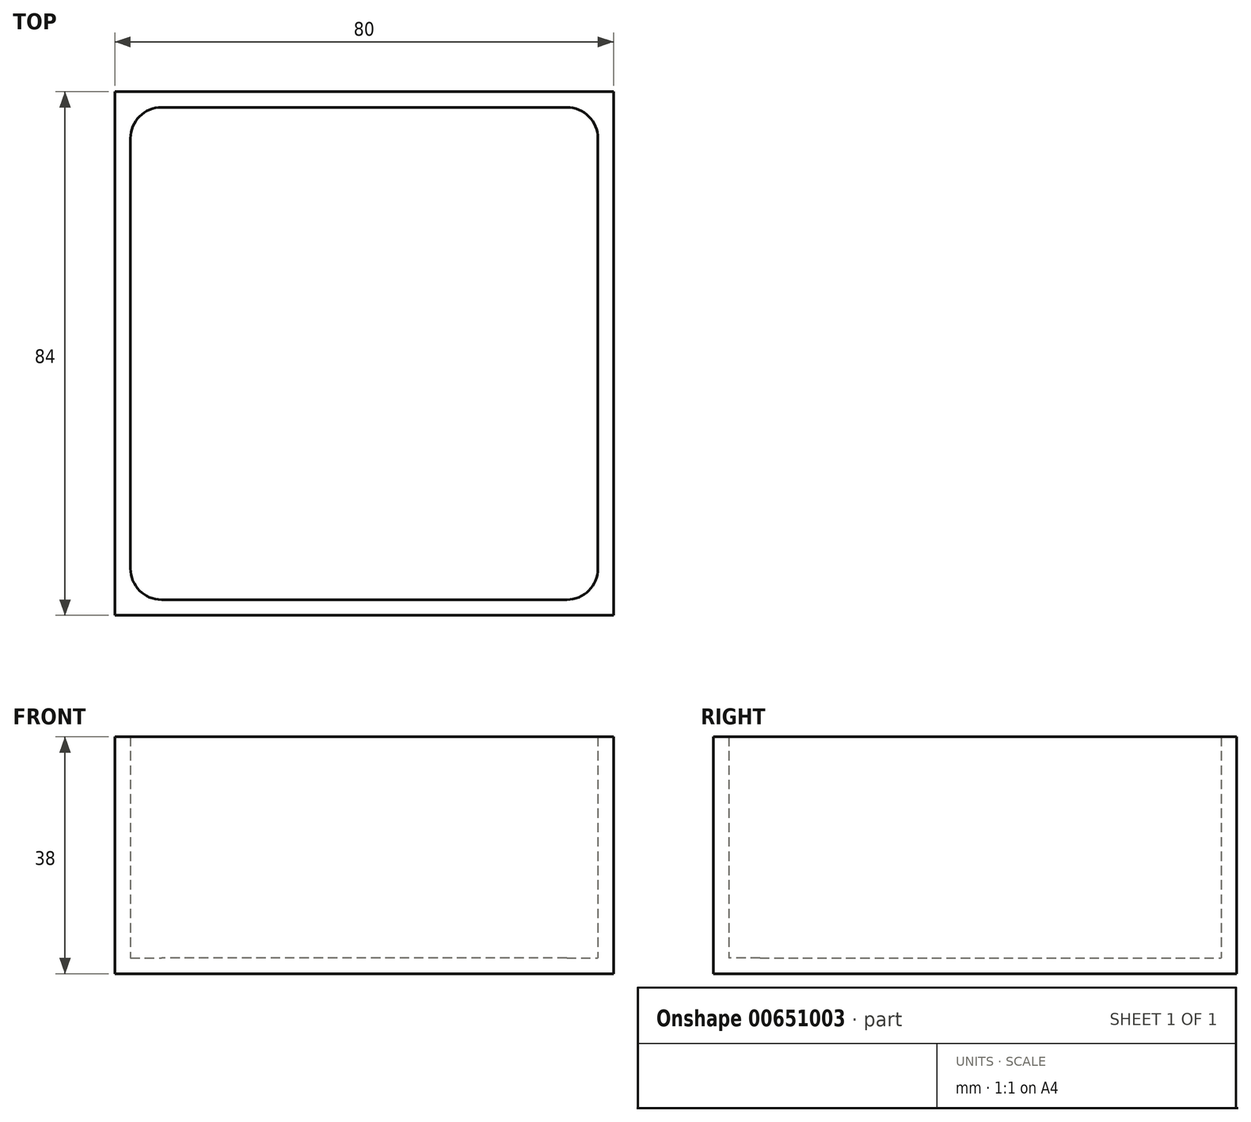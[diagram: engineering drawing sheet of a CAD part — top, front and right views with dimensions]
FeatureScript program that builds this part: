
annotation { "Feature Type Name" : "Feature", "Feature Type Description" : "" }
export const myFeature = defineFeature(function(context is Context, id is Id, definition is map)
    precondition{}
    {
        {
            var Q0;
            Q0=qCreatedBy(makeId("Top.planeOp"),FACE);
            var sketch = newSketch(context, id + "F0", { "sketchPlane" : qUnion([Q0])});
            skLineSegment(sketch, "E0.bottom", {"start": v(0, 0) * mm, "end": v(-80, 0) * mm});
            skLineSegment(sketch, "E0.top", {"start": v(0, 84) * mm, "end": v(-80, 84) * mm});
            skLineSegment(sketch, "E0.left", {"start": v(0, 0) * mm, "end": v(0, 84) * mm});
            skLineSegment(sketch, "E0.right", {"start": v(-80, 0) * mm, "end": v(-80, 84) * mm});
            skSolve(sketch);
        }
        {
            var Q0;
            Q0 = qSketchRegion(id + "F0", true);
            extrude(context, id + "F1", {"entities" : qUnion([Q0]), "depth" : 38 * mm, "offsetDistance" : 25 * mm});
        }
        {
            var Q0;
            Q0=makeQuery(id+"F1.opExtrude","CAP_FACE",FACE,{"disambiguationData":[OSD([sQuery(id+"F0.wireOp",EDGE,"E0.bottom"),sQuery(id+"F0.wireOp",EDGE,"E0.top"),sQuery(id+"F0.wireOp",EDGE,"E0.left"),sQuery(id+"F0.wireOp",EDGE,"E0.right")])],"isStart":false});
            shell(context, id + "F2", {"entities" : qUnion([Q0]), "thickness" : 2.5 * mm});
        }
        {
            var Q0;
            Q0=makeQuery(id+"F2.opShell","OFFSET_EDGE",EDGE,{"disambiguationData":[OSD([sQuery(id+"F0.wireOp",EDGE,"E0.top"),sQuery(id+"F0.wireOp",EDGE,"E0.right")])]});
            var Q1;
            Q1=makeQuery(id+"F2.opShell","OFFSET_EDGE",EDGE,{"disambiguationData":[OSD([sQuery(id+"F0.wireOp",EDGE,"E0.top"),sQuery(id+"F0.wireOp",EDGE,"E0.left")])]});
            var Q2;
            Q2=makeQuery(id+"F2.opShell","OFFSET_EDGE",EDGE,{"disambiguationData":[OSD([sQuery(id+"F0.wireOp",EDGE,"E0.bottom"),sQuery(id+"F0.wireOp",EDGE,"E0.left")])]});
            var Q3;
            Q3=makeQuery(id+"F2.opShell","OFFSET_EDGE",EDGE,{"disambiguationData":[OSD([sQuery(id+"F0.wireOp",EDGE,"E0.bottom"),sQuery(id+"F0.wireOp",EDGE,"E0.right")])]});
            fillet(context, id + "F3", {"entities" : qUnion([Q0, Q1, Q2, Q3]), "radius" : 5 * mm, "tangentPropagation" : true, "allowEdgeOverflow" : false});
        }
    });
